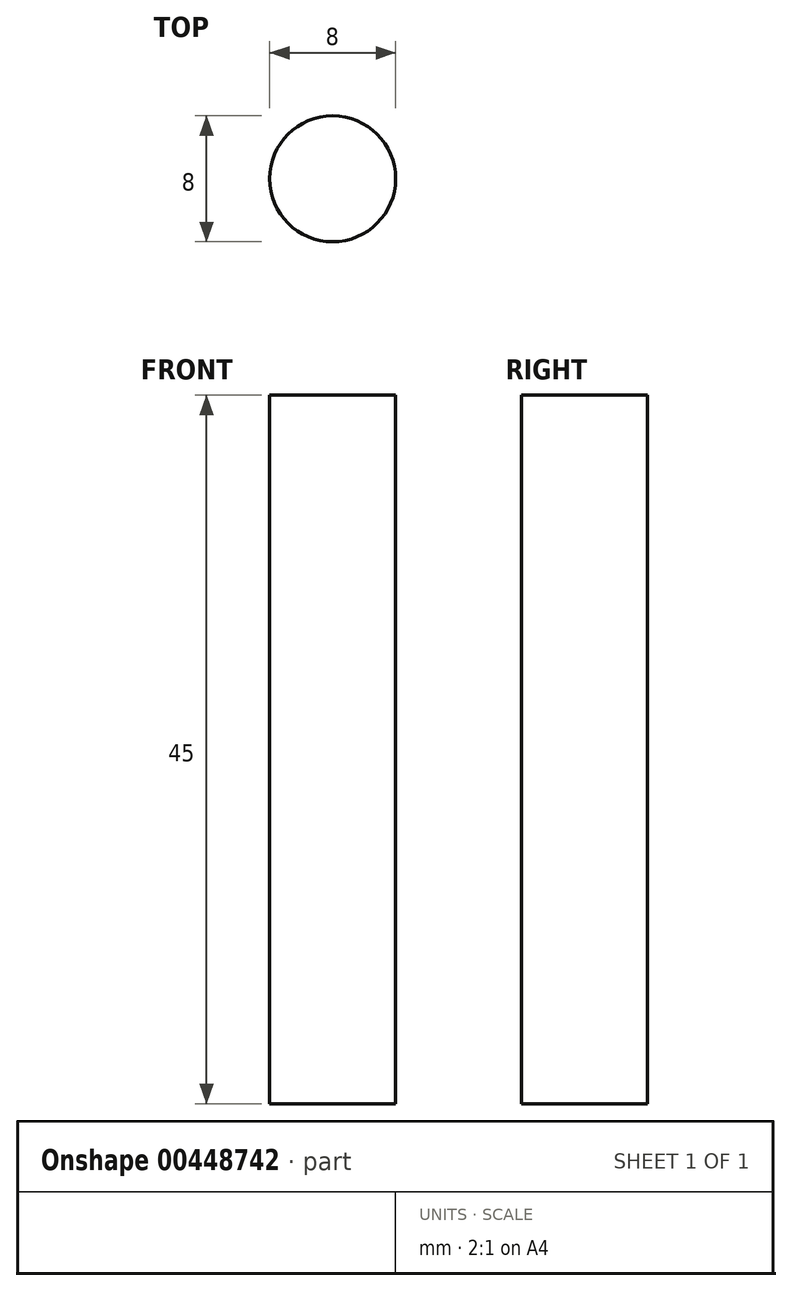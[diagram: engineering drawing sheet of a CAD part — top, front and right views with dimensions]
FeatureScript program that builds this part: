
annotation { "Feature Type Name" : "Feature", "Feature Type Description" : "" }
export const myFeature = defineFeature(function(context is Context, id is Id, definition is map)
    precondition{}
    {
        {
            var Q0;
            Q0=qCreatedBy(makeId("Top.planeOp"),FACE);
            var sketch = newSketch(context, id + "F0", { "sketchPlane" : qUnion([Q0])});
            skCircle(sketch, "E0", {"center": v(0, 0) * mm, "radius": 4 * mm});
            skSolve(sketch);
        }
        {
            var Q0;
            Q0 = qSketchRegion(id + "F0", true);
            extrude(context, id + "F1", {"entities" : qUnion([Q0]), "depth" : 45 * mm});
        }
    });
